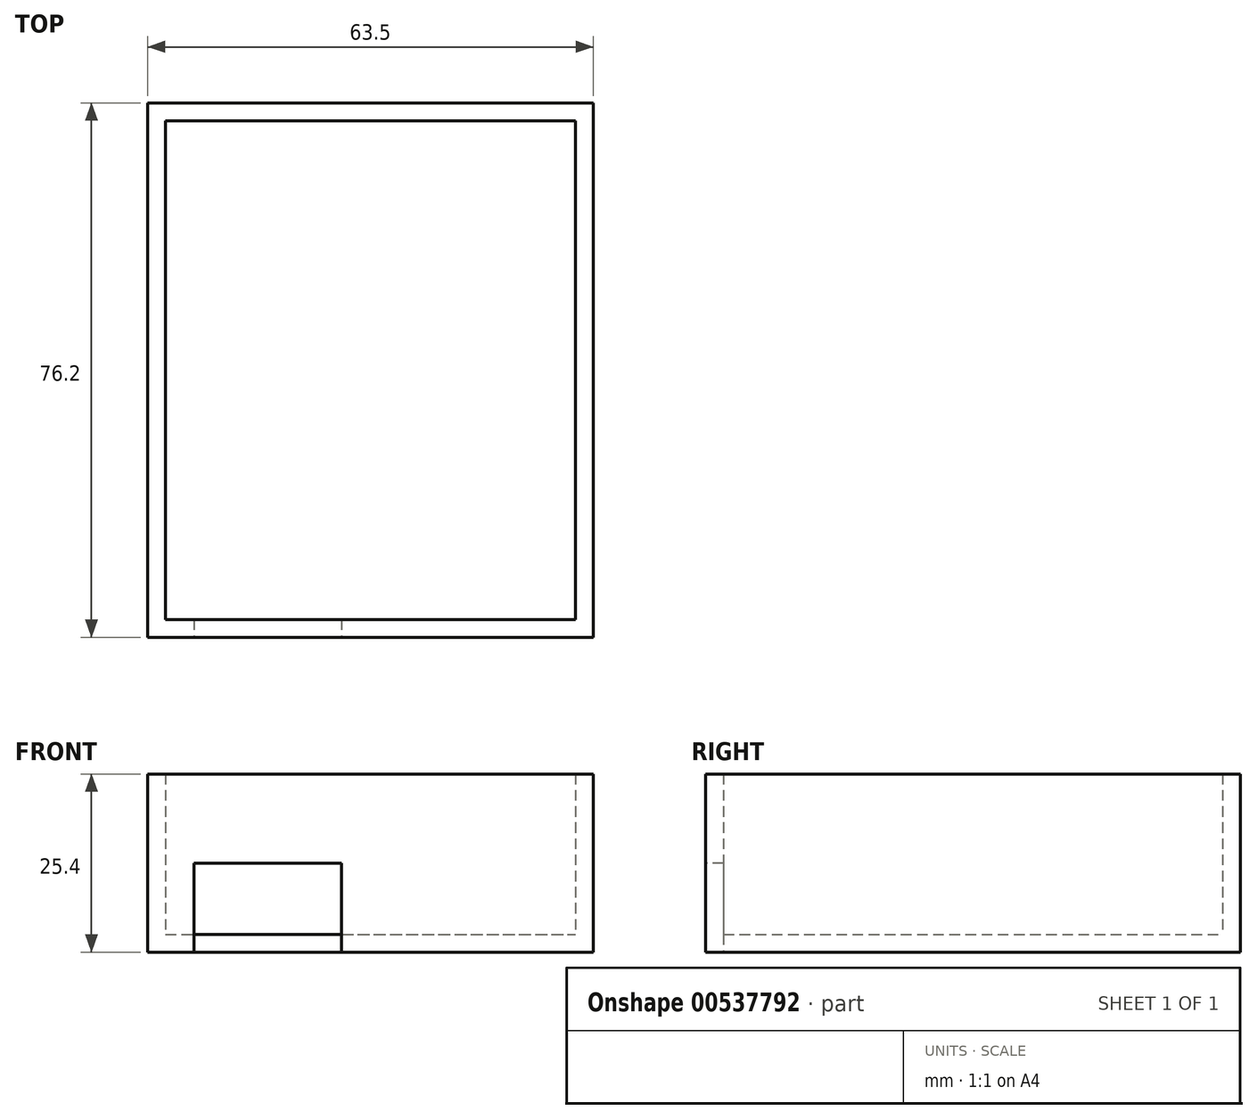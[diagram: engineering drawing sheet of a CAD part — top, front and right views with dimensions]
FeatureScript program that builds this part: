
annotation { "Feature Type Name" : "Feature", "Feature Type Description" : "" }
export const myFeature = defineFeature(function(context is Context, id is Id, definition is map)
    precondition{}
    {
        {
            var Q0;
            Q0=qCreatedBy(makeId("Front.planeOp"),FACE);
            var sketch = newSketch(context, id + "F0", { "sketchPlane" : qUnion([Q0])});
            skLineSegment(sketch, "E0.bottom", {"start": v(-52.13, 25.4) * mm, "end": v(11.37, 25.4) * mm});
            skLineSegment(sketch, "E0.top", {"start": v(-52.13, 0) * mm, "end": v(11.37, 0) * mm});
            skLineSegment(sketch, "E0.left", {"start": v(-52.13, 25.4) * mm, "end": v(-52.13, 0) * mm});
            skLineSegment(sketch, "E0.right", {"start": v(11.37, 25.4) * mm, "end": v(11.37, 0) * mm});
            skSolve(sketch);
        }
        {
            var Q0;
            Q0 = qSketchRegion(id + "F0", true);
            extrude(context, id + "F1", {"entities" : qUnion([Q0]), "endBound" : BoundingType.SYMMETRIC, "depth" : 76.2 * mm, "offsetDistance" : 25.4 * mm});
        }
        {
            var Q0;
            Q0=makeQuery(id+"F1.opExtrude","SWEPT_FACE",FACE,{"disambiguationData":[OSD([sQuery(id+"F0.wireOp",EDGE,"E0.bottom")])]});
            shell(context, id + "F2", {"entities" : qUnion([Q0]), "thickness" : 2.54 * mm});
        }
        {
            var Q0;
            Q0=makeQuery(id+"F1.opExtrude","CAP_FACE",FACE,{"disambiguationData":[OSD([sQuery(id+"F0.wireOp",EDGE,"E0.bottom"),sQuery(id+"F0.wireOp",EDGE,"E0.top"),sQuery(id+"F0.wireOp",EDGE,"E0.left"),sQuery(id+"F0.wireOp",EDGE,"E0.right")])],"isStart":false});
            var sketch = newSketch(context, id + "F3", { "sketchPlane" : qUnion([Q0])});
            skPoint(sketch, "E1.firstSnap0", {"position": v(-52.13, 12.7) * mm});
            skLineSegment(sketch, "E1.bottom", {"start": v(-45.51, 12.7) * mm, "end": v(-24.5, 12.7) * mm});
            skLineSegment(sketch, "E1.top", {"start": v(-45.51, 0) * mm, "end": v(-24.5, 0) * mm});
            skLineSegment(sketch, "E1.left", {"start": v(-45.51, 12.7) * mm, "end": v(-45.51, 0) * mm});
            skLineSegment(sketch, "E1.right", {"start": v(-24.5, 12.7) * mm, "end": v(-24.5, 0) * mm});
            skSolve(sketch);
        }
        {
            var Q0;
            Q0=makeQuery(id+"F3.imprint","IMPRINT",FACE,{"disambiguationData":[TD([[makeQuery(id+"F3.imprint","IMPRINT",EDGE,{"derivedFrom":sQuery(id+"F3.wireOp",EDGE,"E1.bottom")}),-1.0]])]});
            extrude(context, id + "F4", {"entities" : qUnion([Q0]), "operationType" : NewBodyOperationType.REMOVE, "oppositeDirection" : true, "depth" : 2.54 * mm, "offsetDistance" : 25.4 * mm});
        }
    });
